# Revit family: 379990
name_source: partatom
category: Specialty Equipment
revit_build: Autodesk Revit 2018 (Build: 20170223_1515(x64)
units: mm (PartAtom-declared; Revit-internal decimal feet)

## family parameters
Cut with Voids When Loaded = No
Host = Face
OmniClass Number = 23.40.20.21.14
OmniClass Title = Hand and Hair Dryers
Part Type = Normal
Room Calculation Point = No
Round Connector Dimension = Use Diameter
Shared = No

## types (1)
- Recess Kit
    Assembly Code = C1090.4040
    Body = Metal - Excel Dryer - Stainless Stainless - #4 Satin - Finish
    Default Elevation = 2' - 11 1/2"
    Depth = 0' - 3 3/8"
    Description = ADA Compliant Recess Kit
    Frame Height = 2' - 2"
    Frame Width = 1' - 4 3/8"
    Height = 2' - 0 1/8"
    Keynote = 10 28 13
    Manufacturer = Excel Dryer
    Manufacturer Fax Number = 1-413-525-2853
    Model = #40502 Recess Kit
    Product Documentation Link = http://www.exceldryer.com
    Product Name = XLERATOR ADA Compliant Recess Kit
    Product Page URL = http://www.exceldryer.com
    URL = http://www.exceldryer.com
    Version = 2017 - v1.0b
    Width = 1' - 2 3/8"

## geometry (parser evidence)
native form markers: Sweep x2
no freeform markers — native parametric forms only
